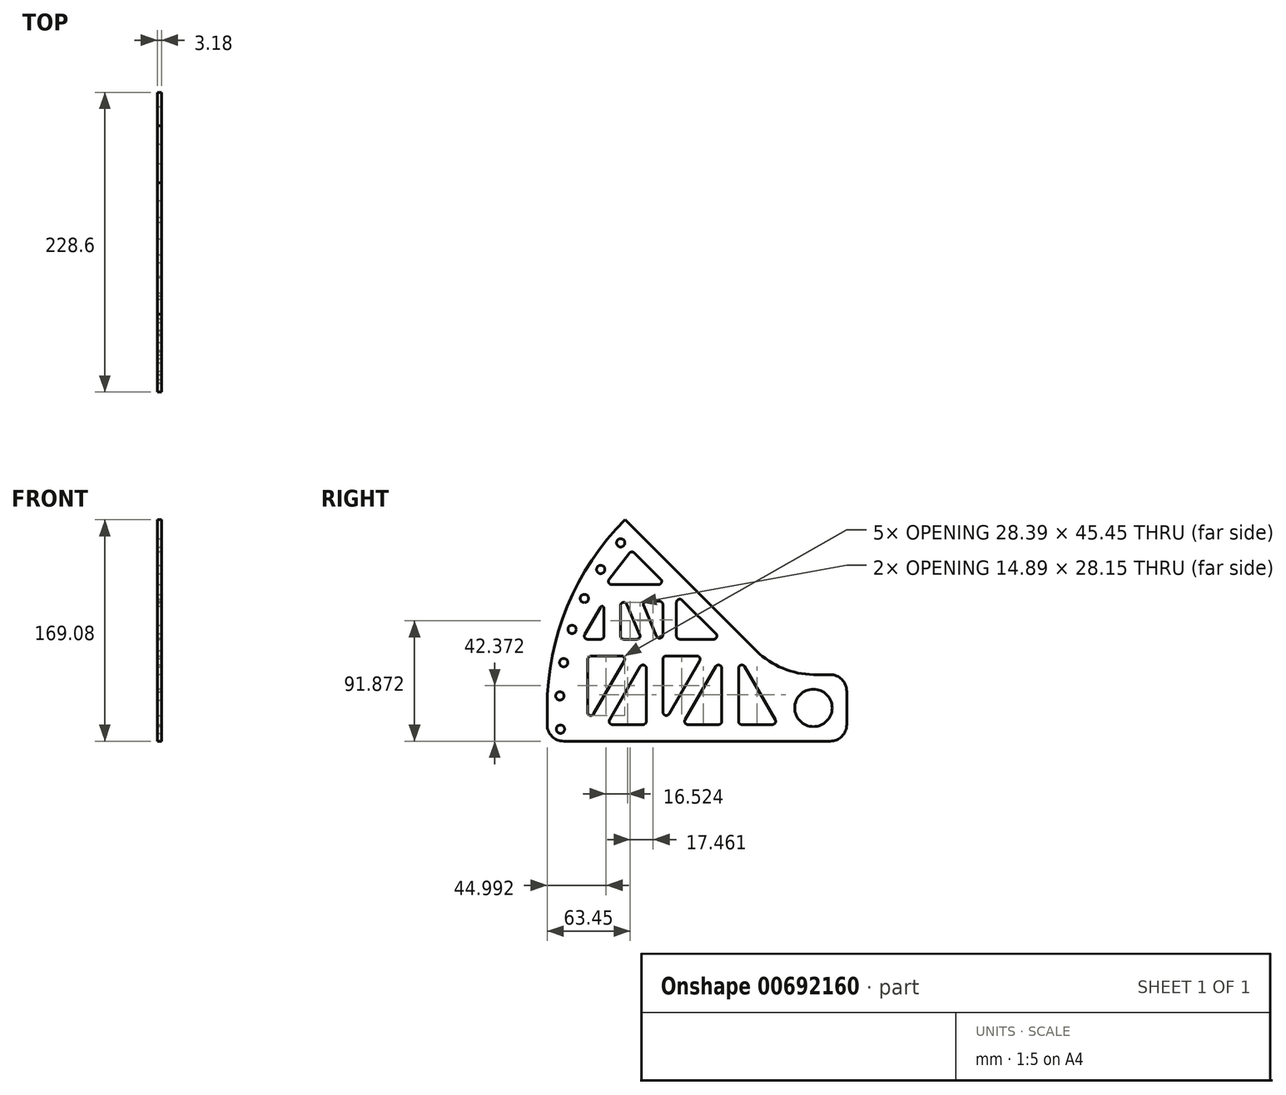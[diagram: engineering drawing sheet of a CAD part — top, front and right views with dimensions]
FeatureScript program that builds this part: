
annotation { "Feature Type Name" : "Feature", "Feature Type Description" : "" }
export const myFeature = defineFeature(function(context is Context, id is Id, definition is map)
    precondition{}
    {
        {
            var Q0;
            Q0=qCreatedBy(makeId("Right.planeOp"),FACE);
            var sketch = newSketch(context, id + "F0", { "sketchPlane" : qUnion([Q0])});
            skLineSegment(sketch, "E0", {"start": v(-203.2, 0) * mm, "end": v(0, 0) * mm, "construction": true});
            skLineSegment(sketch, "E1", {"start": v(25.4, -25.4) * mm, "end": v(25.4, 25.4) * mm, "construction": true});
            skLineSegment(sketch, "E2", {"start": v(25.4, 25.4) * mm, "end": v(-25.4, 25.4) * mm, "construction": true});
            skArc(sketch, "E3", {"start": v(12.7, -25.4) * mm, "mid": v(21.68, -21.68) * mm, "end": v(25.4, -12.7) * mm});
            skArc(sketch, "E4", {"start": v(25.4, 12.7) * mm, "mid": v(21.68, 21.68) * mm, "end": v(12.7, 25.4) * mm});
            skArc(sketch, "E5", {"start": v(-43.36, 43.36) * mm, "mid": v(-23.4, 30.23) * mm, "end": v(0, 25.4) * mm});
            skLineSegment(sketch, "E6", {"start": v(25.4, 12.7) * mm, "end": v(25.4, -12.7) * mm});
            skLineSegment(sketch, "E7", {"start": v(-143.68, 143.68) * mm, "end": v(-43.36, 43.36) * mm});
            skLineSegment(sketch, "E8", {"start": v(0, 25.4) * mm, "end": v(12.7, 25.4) * mm});
            skCircle(sketch, "E9", {"center": v(0, 0) * mm, "radius": 14.29 * mm});
            skLineSegment(sketch, "E10", {"start": v(12.7, -25.4) * mm, "end": v(-203.2, -25.4) * mm, "construction": true});
            skArc(sketch, "E11", {"start": v(-203.2, -12.7) * mm, "mid": v(-199.48, -21.68) * mm, "end": v(-190.5, -25.4) * mm});
            skLineSegment(sketch, "E12", {"start": v(-203.2, 0) * mm, "end": v(-203.2, -12.7) * mm});
            skArc(sketch, "E13", {"start": v(-203.2, 0) * mm, "mid": v(-187.73, 77.76) * mm, "end": v(-143.68, 143.68) * mm});
            skLineSegment(sketch, "E14", {"start": v(-190.5, -25.4) * mm, "end": v(12.7, -25.4) * mm});
            skSolve(sketch);
        }
        {
            var Q0;
            Q0=makeQuery(id+"F0.imprint","IMPRINT",FACE,{"disambiguationData":[TD([[makeQuery(id+"F0.imprint","IMPRINT",EDGE,{"derivedFrom":sQuery(id+"F0.wireOp",EDGE,"E3")}),1.0]])]});
            extrude(context, id + "F1", {"entities" : qUnion([Q0]), "depth" : 3.17 * mm, "offsetDistance" : 25.4 * mm});
        }
        {
            var Q0;
            Q0=makeQuery(id+"F1.opExtrude","CAP_FACE",FACE,{"disambiguationData":[OSD([sQuery(id+"F0.wireOp",EDGE,"E3"),sQuery(id+"F0.wireOp",EDGE,"E4"),sQuery(id+"F0.wireOp",EDGE,"E5"),sQuery(id+"F0.wireOp",EDGE,"E6"),sQuery(id+"F0.wireOp",EDGE,"E7"),sQuery(id+"F0.wireOp",EDGE,"E8"),sQuery(id+"F0.wireOp",EDGE,"E9"),sQuery(id+"F0.wireOp",EDGE,"E11"),sQuery(id+"F0.wireOp",EDGE,"E12"),sQuery(id+"F0.wireOp",EDGE,"E13"),sQuery(id+"F0.wireOp",EDGE,"E14")])],"isStart":false});
            var sketch = newSketch(context, id + "F2", { "sketchPlane" : qUnion([Q0])});
            skCircle(sketch, "E15", {"center": v(0, 0) * mm, "radius": 190.5 * mm, "construction": true});
            skCircle(sketch, "E16", {"center": v(0, 0) * mm, "radius": 193.68 * mm, "construction": true});
            skPoint(sketch, "E17", {"position": v(-147.06, 126.02) * mm});
            skPoint(sketch, "E18", {"position": v(-162.3, 105.7) * mm});
            skPoint(sketch, "E19", {"position": v(-174.73, 83.55) * mm});
            skPoint(sketch, "E20", {"position": v(-184.16, 59.96) * mm});
            skPoint(sketch, "E21", {"position": v(-190.57, 34.56) * mm});
            skPoint(sketch, "E22", {"position": v(-193.46, 9.16) * mm});
            skPoint(sketch, "E23", {"position": v(-193, -16.24) * mm});
            skCircle(sketch, "E24", {"center": v(-193, -16.24) * mm, "radius": 3.17 * mm});
            skCircle(sketch, "E25", {"center": v(-193.46, 9.16) * mm, "radius": 3.17 * mm});
            skCircle(sketch, "E26", {"center": v(-147.06, 126.02) * mm, "radius": 3.18 * mm});
            skCircle(sketch, "E27", {"center": v(-162.3, 105.7) * mm, "radius": 3.17 * mm});
            skCircle(sketch, "E28", {"center": v(-174.73, 83.55) * mm, "radius": 3.18 * mm});
            skCircle(sketch, "E29", {"center": v(-184.16, 59.96) * mm, "radius": 3.17 * mm});
            skCircle(sketch, "E30", {"center": v(-190.57, 34.56) * mm, "radius": 3.17 * mm});
            skSolve(sketch);
        }
        {
            var Q0;
            Q0 = qSketchRegion(id + "F2", true);
            extrude(context, id + "F3", {"entities" : qUnion([Q0]), "operationType" : NewBodyOperationType.REMOVE, "oppositeDirection" : true, "depth" : 25.4 * mm, "offsetDistance" : 25.4 * mm});
        }
        {
            var Q0;
            Q0=makeQuery(id+"F1.opExtrude","CAP_FACE",FACE,{"disambiguationData":[OSD([sQuery(id+"F0.wireOp",EDGE,"E3"),sQuery(id+"F0.wireOp",EDGE,"E4"),sQuery(id+"F0.wireOp",EDGE,"E5"),sQuery(id+"F0.wireOp",EDGE,"E6"),sQuery(id+"F0.wireOp",EDGE,"E7"),sQuery(id+"F0.wireOp",EDGE,"E8"),sQuery(id+"F0.wireOp",EDGE,"E9"),sQuery(id+"F0.wireOp",EDGE,"E11"),sQuery(id+"F0.wireOp",EDGE,"E12"),sQuery(id+"F0.wireOp",EDGE,"E13"),sQuery(id+"F0.wireOp",EDGE,"E14")])],"isStart":false});
            var sketch = newSketch(context, id + "F4", { "sketchPlane" : qUnion([Q0])});
            skLineSegment(sketch, "E31", {"start": v(-14.29, 0) * mm, "end": v(-26.99, 0) * mm, "construction": true});
            skLineSegment(sketch, "E32", {"start": v(-93.52, 93.52) * mm, "end": v(-102.5, 84.54) * mm, "construction": true});
            skLineSegment(sketch, "E33", {"start": v(-26.92, 9.77) * mm, "end": v(-26.92, -12.7) * mm, "construction": true});
            skLineSegment(sketch, "E34", {"start": v(-57.17, 30.22) * mm, "end": v(-57.17, -10.16) * mm});
            skLineSegment(sketch, "E35", {"start": v(-54.63, -12.7) * mm, "end": v(-31.32, -12.7) * mm});
            skLineSegment(sketch, "E36", {"start": v(-52.43, 31.49) * mm, "end": v(-29.12, -8.9) * mm});
            skLineSegment(sketch, "E37", {"start": v(-69.87, -10.16) * mm, "end": v(-69.87, 30.22) * mm});
            skLineSegment(sketch, "E38", {"start": v(-74.6, 31.49) * mm, "end": v(-97.92, -8.9) * mm});
            skLineSegment(sketch, "E39", {"start": v(-95.72, -12.7) * mm, "end": v(-72.4, -12.7) * mm});
            skLineSegment(sketch, "E40", {"start": v(-85, 13.5) * mm, "end": v(-96, 19.85) * mm, "construction": true});
            skLineSegment(sketch, "E41", {"start": v(-96, 19.85) * mm, "end": v(-114.79, -12.7) * mm, "construction": true});
            skLineSegment(sketch, "E42", {"start": v(-110.05, -4.5) * mm, "end": v(-86.73, 35.89) * mm});
            skLineSegment(sketch, "E43", {"start": v(-88.93, 39.7) * mm, "end": v(-112.25, 39.7) * mm});
            skLineSegment(sketch, "E44", {"start": v(-114.79, 37.16) * mm, "end": v(-114.79, -3.22) * mm});
            skLineSegment(sketch, "E45", {"start": v(-127.49, 30.22) * mm, "end": v(-127.49, -10.16) * mm});
            skLineSegment(sketch, "E46", {"start": v(-130.03, -12.7) * mm, "end": v(-153.34, -12.7) * mm});
            skLineSegment(sketch, "E47", {"start": v(-155.54, -8.9) * mm, "end": v(-132.23, 31.49) * mm});
            skLineSegment(sketch, "E48", {"start": v(-172.4, 36.52) * mm, "end": v(-172.4, -3.22) * mm});
            skLineSegment(sketch, "E49", {"start": v(-167.66, -4.5) * mm, "end": v(-144.35, 35.89) * mm});
            skLineSegment(sketch, "E50", {"start": v(-146.55, 39.7) * mm, "end": v(-169.23, 39.7) * mm});
            skLineSegment(sketch, "E51", {"start": v(-155.26, 39.7) * mm, "end": v(-155.26, 52.4) * mm, "construction": true});
            skPoint(sketch, "E52", {"position": v(-155.26, 52.4) * mm});
            skPoint(sketch, "E53", {"position": v(-127.71, 81.39) * mm});
            skPoint(sketch, "E53.positionSnap0", {"position": v(-127.71, 103.2) * mm});
            skLineSegment(sketch, "E54", {"start": v(-174.45, 56.21) * mm, "end": v(-162.5, 76.9) * mm});
            skLineSegment(sketch, "E55", {"start": v(-162.44, 52.4) * mm, "end": v(-172.26, 52.4) * mm});
            skLineSegment(sketch, "E56", {"start": v(-159.9, 76.2) * mm, "end": v(-159.9, 54.94) * mm});
            skLineSegment(sketch, "E57", {"start": v(-147.2, 70.46) * mm, "end": v(-147.2, 90.5) * mm, "construction": true});
            skLineSegment(sketch, "E58", {"start": v(-147.2, 78.03) * mm, "end": v(-147.2, 54.94) * mm});
            skLineSegment(sketch, "E59", {"start": v(-144.66, 52.4) * mm, "end": v(-134.84, 52.4) * mm});
            skLineSegment(sketch, "E60", {"start": v(-132.5, 55.93) * mm, "end": v(-142.32, 79.02) * mm});
            skLineSegment(sketch, "E61", {"start": v(-128.7, 75.87) * mm, "end": v(-131.05, 81.39) * mm, "construction": true});
            skLineSegment(sketch, "E62", {"start": v(-129.54, 77.86) * mm, "end": v(-119.72, 54.77) * mm});
            skLineSegment(sketch, "E63", {"start": v(-114.84, 55.76) * mm, "end": v(-114.84, 78.85) * mm});
            skLineSegment(sketch, "E64", {"start": v(-117.38, 81.39) * mm, "end": v(-127.2, 81.39) * mm});
            skLineSegment(sketch, "E65", {"start": v(-104.5, 71.45) * mm, "end": v(-104.5, 52.4) * mm, "construction": true});
            skLineSegment(sketch, "E66", {"start": v(-104.5, 54.94) * mm, "end": v(-104.5, 80.43) * mm});
            skLineSegment(sketch, "E67", {"start": v(-100.17, 82.23) * mm, "end": v(-74.4, 56.74) * mm});
            skLineSegment(sketch, "E68", {"start": v(-101.95, 52.4) * mm, "end": v(-76.19, 52.4) * mm});
            skPoint(sketch, "E69.visualSharp", {"position": v(-172.4, 39.7) * mm});
            skArc(sketch, "E69.filletArc", {"start": v(-169.23, 39.7) * mm, "mid": v(-171.47, 38.77) * mm, "end": v(-172.4, 36.52) * mm});
            skPoint(sketch, "E70.visualSharp", {"position": v(-172.4, -12.7) * mm});
            skArc(sketch, "E70.filletArc", {"start": v(-172.4, -3.22) * mm, "mid": v(-170.52, -5.67) * mm, "end": v(-167.66, -4.5) * mm});
            skPoint(sketch, "E71.visualSharp", {"position": v(-142.15, 39.7) * mm});
            skArc(sketch, "E71.filletArc", {"start": v(-144.35, 35.89) * mm, "mid": v(-144.35, 38.43) * mm, "end": v(-146.55, 39.7) * mm});
            skPoint(sketch, "E72.visualSharp", {"position": v(-127.49, 39.7) * mm});
            skArc(sketch, "E72.filletArc", {"start": v(-127.49, 30.22) * mm, "mid": v(-129.37, 32.67) * mm, "end": v(-132.23, 31.49) * mm});
            skPoint(sketch, "E73.visualSharp", {"position": v(-127.49, -12.7) * mm});
            skArc(sketch, "E73.filletArc", {"start": v(-130.03, -12.7) * mm, "mid": v(-128.23, -11.96) * mm, "end": v(-127.49, -10.16) * mm});
            skPoint(sketch, "E74.visualSharp", {"position": v(-157.74, -12.7) * mm});
            skArc(sketch, "E74.filletArc", {"start": v(-155.54, -8.9) * mm, "mid": v(-155.54, -11.43) * mm, "end": v(-153.34, -12.7) * mm});
            skPoint(sketch, "E75.visualSharp", {"position": v(-114.79, 39.7) * mm});
            skArc(sketch, "E75.filletArc", {"start": v(-112.25, 39.7) * mm, "mid": v(-114.04, 38.96) * mm, "end": v(-114.79, 37.16) * mm});
            skPoint(sketch, "E76.visualSharp", {"position": v(-84.53, 39.7) * mm});
            skArc(sketch, "E76.filletArc", {"start": v(-86.73, 35.89) * mm, "mid": v(-86.73, 38.43) * mm, "end": v(-88.93, 39.7) * mm});
            skPoint(sketch, "E77.visualSharp", {"position": v(-114.79, -12.7) * mm});
            skArc(sketch, "E77.filletArc", {"start": v(-114.79, -3.22) * mm, "mid": v(-112.9, -5.67) * mm, "end": v(-110.05, -4.5) * mm});
            skPoint(sketch, "E78.visualSharp", {"position": v(-69.87, 39.7) * mm});
            skArc(sketch, "E78.filletArc", {"start": v(-69.87, 30.22) * mm, "mid": v(-71.75, 32.67) * mm, "end": v(-74.6, 31.49) * mm});
            skPoint(sketch, "E79.visualSharp", {"position": v(-69.87, -12.7) * mm});
            skArc(sketch, "E79.filletArc", {"start": v(-72.4, -12.7) * mm, "mid": v(-70.61, -11.96) * mm, "end": v(-69.87, -10.16) * mm});
            skPoint(sketch, "E80.visualSharp", {"position": v(-57.17, -12.7) * mm});
            skArc(sketch, "E80.filletArc", {"start": v(-57.17, -10.16) * mm, "mid": v(-56.43, -11.96) * mm, "end": v(-54.63, -12.7) * mm});
            skPoint(sketch, "E81.visualSharp", {"position": v(-57.17, 39.7) * mm});
            skArc(sketch, "E81.filletArc", {"start": v(-52.43, 31.49) * mm, "mid": v(-55.29, 32.67) * mm, "end": v(-57.17, 30.22) * mm});
            skPoint(sketch, "E82.visualSharp", {"position": v(-26.92, -12.7) * mm});
            skArc(sketch, "E82.filletArc", {"start": v(-31.32, -12.7) * mm, "mid": v(-29.12, -11.43) * mm, "end": v(-29.12, -8.9) * mm});
            skPoint(sketch, "E83.visualSharp", {"position": v(-100.12, -12.7) * mm});
            skArc(sketch, "E83.filletArc", {"start": v(-97.92, -8.9) * mm, "mid": v(-97.92, -11.43) * mm, "end": v(-95.72, -12.7) * mm});
            skPoint(sketch, "E84.visualSharp", {"position": v(-104.5, 52.4) * mm});
            skArc(sketch, "E84.filletArc", {"start": v(-104.5, 54.94) * mm, "mid": v(-103.75, 53.14) * mm, "end": v(-101.95, 52.4) * mm});
            skPoint(sketch, "E85.visualSharp", {"position": v(-104.5, 86.51) * mm});
            skArc(sketch, "E85.filletArc", {"start": v(-100.17, 82.23) * mm, "mid": v(-102.93, 82.77) * mm, "end": v(-104.5, 80.43) * mm});
            skPoint(sketch, "E86.visualSharp", {"position": v(-70, 52.4) * mm});
            skArc(sketch, "E86.filletArc", {"start": v(-76.19, 52.4) * mm, "mid": v(-73.84, 53.97) * mm, "end": v(-74.4, 56.74) * mm});
            skPoint(sketch, "E87.visualSharp", {"position": v(-114.84, 81.39) * mm});
            skArc(sketch, "E87.filletArc", {"start": v(-114.84, 78.85) * mm, "mid": v(-115.59, 80.65) * mm, "end": v(-117.38, 81.39) * mm});
            skPoint(sketch, "E88.visualSharp", {"position": v(-131.05, 81.39) * mm});
            skArc(sketch, "E88.filletArc", {"start": v(-127.2, 81.39) * mm, "mid": v(-129.32, 80.25) * mm, "end": v(-129.54, 77.86) * mm});
            skPoint(sketch, "E89.visualSharp", {"position": v(-114.84, 43.3) * mm});
            skArc(sketch, "E89.filletArc", {"start": v(-119.72, 54.77) * mm, "mid": v(-116.88, 53.27) * mm, "end": v(-114.84, 55.76) * mm});
            skPoint(sketch, "E90.visualSharp", {"position": v(-131, 52.4) * mm});
            skArc(sketch, "E90.filletArc", {"start": v(-134.84, 52.4) * mm, "mid": v(-132.72, 53.54) * mm, "end": v(-132.5, 55.93) * mm});
            skPoint(sketch, "E91.visualSharp", {"position": v(-147.2, 52.4) * mm});
            skArc(sketch, "E91.filletArc", {"start": v(-147.2, 54.94) * mm, "mid": v(-146.45, 53.14) * mm, "end": v(-144.66, 52.4) * mm});
            skPoint(sketch, "E92.visualSharp", {"position": v(-159.9, 81.39) * mm});
            skArc(sketch, "E92.filletArc", {"start": v(-159.9, 76.2) * mm, "mid": v(-160.93, 77.54) * mm, "end": v(-162.5, 76.9) * mm});
            skPoint(sketch, "E93.visualSharp", {"position": v(-176.66, 52.4) * mm});
            skArc(sketch, "E93.filletArc", {"start": v(-174.45, 56.21) * mm, "mid": v(-174.46, 53.67) * mm, "end": v(-172.26, 52.4) * mm});
            skPoint(sketch, "E94.visualSharp", {"position": v(-159.9, 52.4) * mm});
            skArc(sketch, "E94.filletArc", {"start": v(-162.44, 52.4) * mm, "mid": v(-160.64, 53.14) * mm, "end": v(-159.9, 54.94) * mm});
            skPoint(sketch, "E95.visualSharp", {"position": v(-147.2, 90.5) * mm});
            skArc(sketch, "E95.filletArc", {"start": v(-142.32, 79.02) * mm, "mid": v(-145.16, 80.52) * mm, "end": v(-147.2, 78.03) * mm});
            skLineSegment(sketch, "E96", {"start": v(-123.4, 81.39) * mm, "end": v(-123.4, 94.09) * mm, "construction": true});
            skLineSegment(sketch, "E97", {"start": v(-123.4, 94.09) * mm, "end": v(-112.15, 94.09) * mm, "construction": true});
            skLineSegment(sketch, "E98", {"start": v(-118.33, 94.09) * mm, "end": v(-153.85, 94.09) * mm});
            skLineSegment(sketch, "E99", {"start": v(-140.52, 118.13) * mm, "end": v(-155.86, 98.18) * mm});
            skLineSegment(sketch, "E100", {"start": v(-136.72, 118.39) * mm, "end": v(-116.55, 98.44) * mm});
            skPoint(sketch, "E101.visualSharp", {"position": v(-159, 94.09) * mm});
            skArc(sketch, "E101.filletArc", {"start": v(-155.86, 98.18) * mm, "mid": v(-156.13, 95.5) * mm, "end": v(-153.85, 94.09) * mm});
            skPoint(sketch, "E102.visualSharp", {"position": v(-138.77, 120.41) * mm});
            skArc(sketch, "E102.filletArc", {"start": v(-136.72, 118.39) * mm, "mid": v(-138.68, 119.12) * mm, "end": v(-140.52, 118.13) * mm});
            skPoint(sketch, "E103.visualSharp", {"position": v(-112.15, 94.09) * mm});
            skArc(sketch, "E103.filletArc", {"start": v(-118.33, 94.09) * mm, "mid": v(-115.98, 95.66) * mm, "end": v(-116.55, 98.44) * mm});
            skSolve(sketch);
        }
        {
            var Q0;
            Q0 = qSketchRegion(id + "F4", true);
            extrude(context, id + "F5", {"entities" : qUnion([Q0]), "operationType" : NewBodyOperationType.REMOVE, "oppositeDirection" : true, "depth" : 25.4 * mm, "offsetDistance" : 25.4 * mm});
        }
    });
